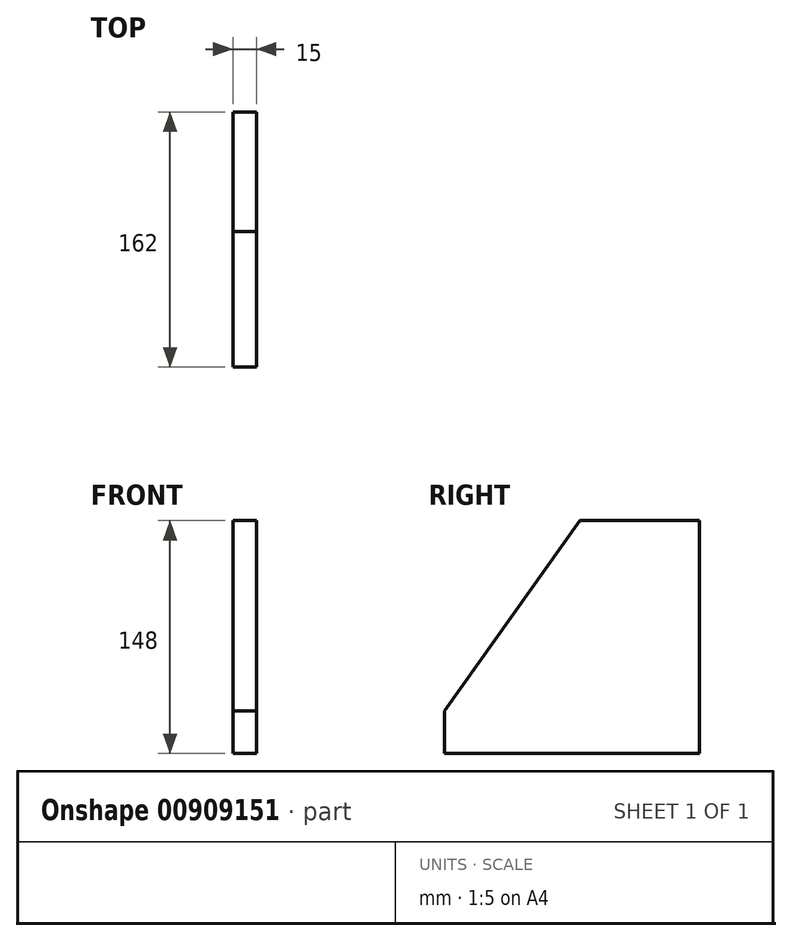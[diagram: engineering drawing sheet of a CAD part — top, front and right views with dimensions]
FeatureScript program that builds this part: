
annotation { "Feature Type Name" : "Feature", "Feature Type Description" : "" }
export const myFeature = defineFeature(function(context is Context, id is Id, definition is map)
    precondition{}
    {
        {
            var Q0;
            Q0=qCreatedBy(makeId("Right.planeOp"),FACE);
            var sketch = newSketch(context, id + "F0", { "sketchPlane" : qUnion([Q0])});
            skLineSegment(sketch, "E0.bottom", {"start": v(81, -74) * mm, "end": v(-81, -74) * mm});
            skLineSegment(sketch, "E0.top", {"start": v(81, 74) * mm, "end": v(-81, 74) * mm});
            skLineSegment(sketch, "E0.left", {"start": v(81, -74) * mm, "end": v(81, 74) * mm});
            skLineSegment(sketch, "E0.right", {"start": v(-81, -74) * mm, "end": v(-81, 74) * mm});
            skPoint(sketch, "E0.middle", {"position": v(0, 0) * mm});
            skLineSegment(sketch, "E1", {"start": v(5, 74) * mm, "end": v(-81, -47) * mm});
            skSolve(sketch);
        }
        {
            var Q0;
            Q0=makeQuery(id+"F0.imprint","IMPRINT",FACE,{"disambiguationData":[TD([[makeQuery(id+"F0.imprint","IMPRINT",EDGE,{"derivedFrom":sQuery(id+"F0.wireOp",EDGE,"E0.bottom")}),-1.0]])]});
            extrude(context, id + "F1", {"entities" : qUnion([Q0]), "depth" : 15 * mm, "offsetDistance" : 25 * mm});
        }
    });
